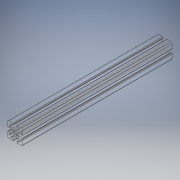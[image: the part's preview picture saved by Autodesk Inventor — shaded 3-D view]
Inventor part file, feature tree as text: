
AUTODESK INVENTOR PART (.ipt)
format: ipt  version: 2019 (Build 230136000, 136)  size: 235,008 bytes
history: native  units: in
note: dims shown in document units (in); Inventor stores cm internally (conversion verified against a paired STEP export)
features: plane x1, extrude x1, sketch x1
ambient origin geometry x8: Origin, YZ Plane, XZ Plane, XY Plane, X Axis, Y Axis, Z Axis, Center Point
bodies: Solid1 (feature_tree)
feature tree (3):
  plane  "Work Plane1"
  extrude  "Extrusion1"  [1 undecoded]
  sketch  "Sketch1"  dims[d0=14.75in d1=0.0in]
note: 1 required parameter value undecoded (feature->parameter linkage not recoverable at this tier; creation-order binding heuristic only, values carry confidence <= 0.55)
